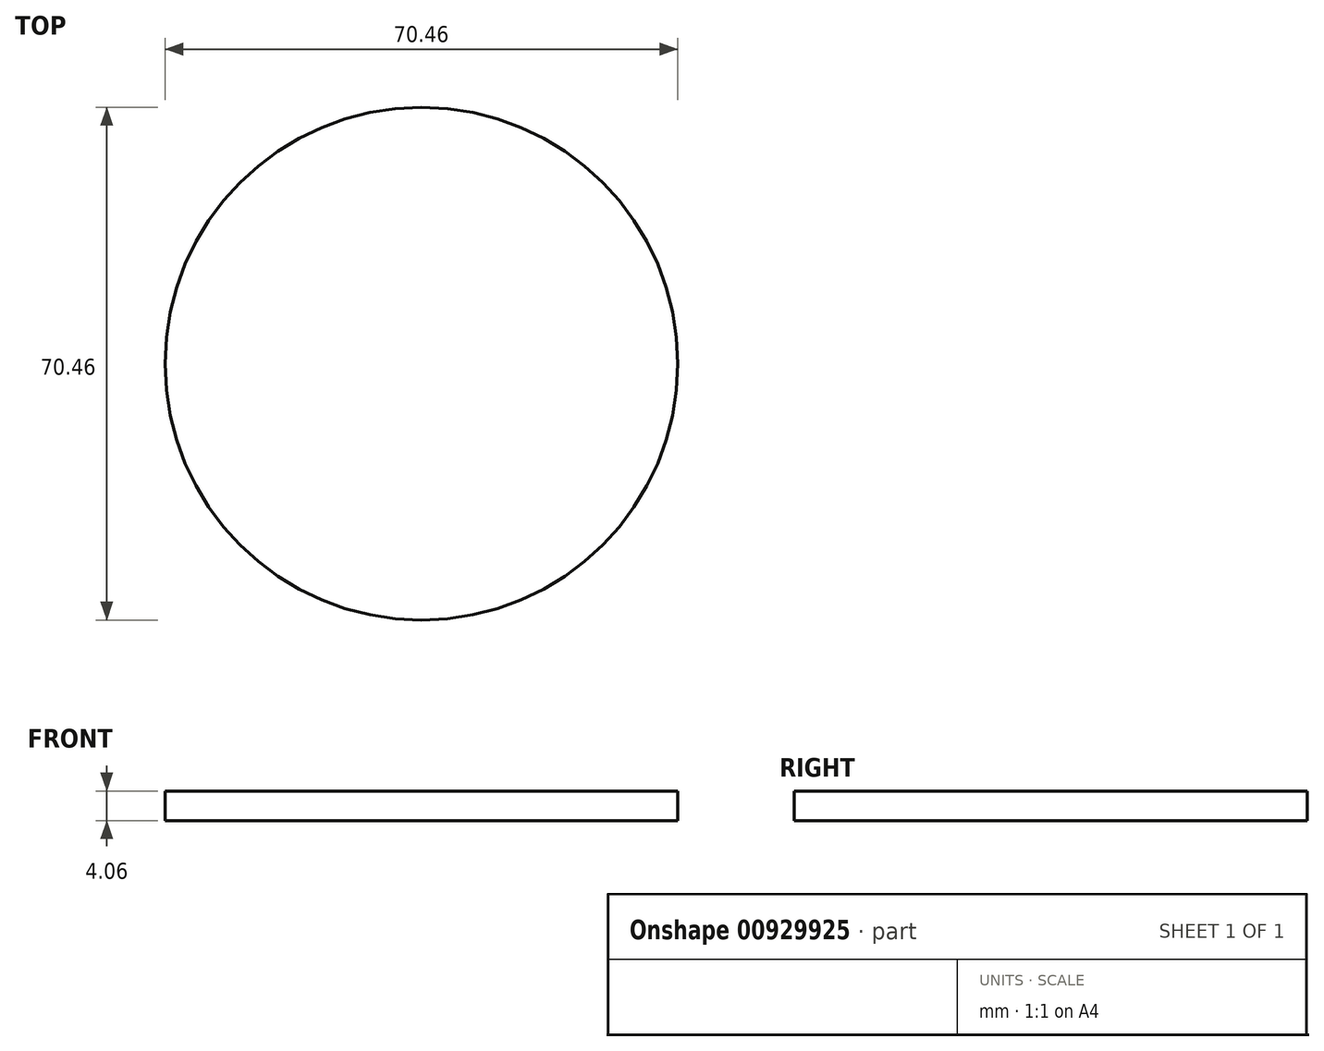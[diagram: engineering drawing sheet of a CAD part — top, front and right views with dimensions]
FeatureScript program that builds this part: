
annotation { "Feature Type Name" : "Feature", "Feature Type Description" : "" }
export const myFeature = defineFeature(function(context is Context, id is Id, definition is map)
    precondition{}
    {
        {
            var Q0;
            Q0=qCreatedBy(makeId("Top.planeOp"),FACE);
            var sketch = newSketch(context, id + "F0", { "sketchPlane" : qUnion([Q0])});
            skCircle(sketch, "E0", {"center": v(0, 0) * mm, "radius": 35.23 * mm});
            skSolve(sketch);
        }
        {
            var Q0;
            Q0=makeQuery(id+"F0.imprint","IMPRINT",FACE,{"disambiguationData":[TD([[makeQuery(id+"F0.imprint","IMPRINT",EDGE,{"derivedFrom":sQuery(id+"F0.wireOp",EDGE,"E0")}),1.0]])]});
            extrude(context, id + "F1", {"entities" : qUnion([Q0]), "depth" : 4.06 * mm, "offsetDistance" : 25.4 * mm});
        }
    });
